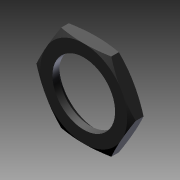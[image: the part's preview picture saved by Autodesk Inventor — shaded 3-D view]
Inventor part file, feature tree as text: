
AUTODESK INVENTOR PART (.ipt)
format: ipt  version: 2011 SP1 (Build 150282100, 282)  size: 118,272 bytes
history: native  units: in
note: dims shown in document units (in); Inventor stores cm internally (conversion verified against a paired STEP export)
features: other x7, sketch x3, revolve x1, extrude x1, hole x1
ambient origin geometry x8: Origin, YZ Plane, XZ Plane, XY Plane, X Axis, Y Axis, Z Axis, Center Point
bodies: Solid1 (feature_tree)
feature tree (13):
  revolve  "Revolution1"  [1 undecoded]
  extrude  "Extrusion1"  [1 undecoded]
  hole  "Drilling 1"  [1 undecoded]
  other  "nut_XY"
  other  "nut_YZ"
  other  "nut_ZX"
  other  "nut_X"
  other  "nut_Y"
  other  "nut_Z"
  other  "nut_Center"
  sketch  "Sketch_1"  dims[d0=360.0deg d1=0.158in d2=0.0in]
  sketch  "Sketch_2"  dims[d3=0.3979in d4=0.75in d5=0.472in d6=0.25in d7=0.6184in d8=0.079in d9=0.0in]
  sketch  "Sketch3"
note: 3 required parameter values undecoded (feature->parameter linkage not recoverable at this tier; creation-order binding heuristic only, values carry confidence <= 0.55)